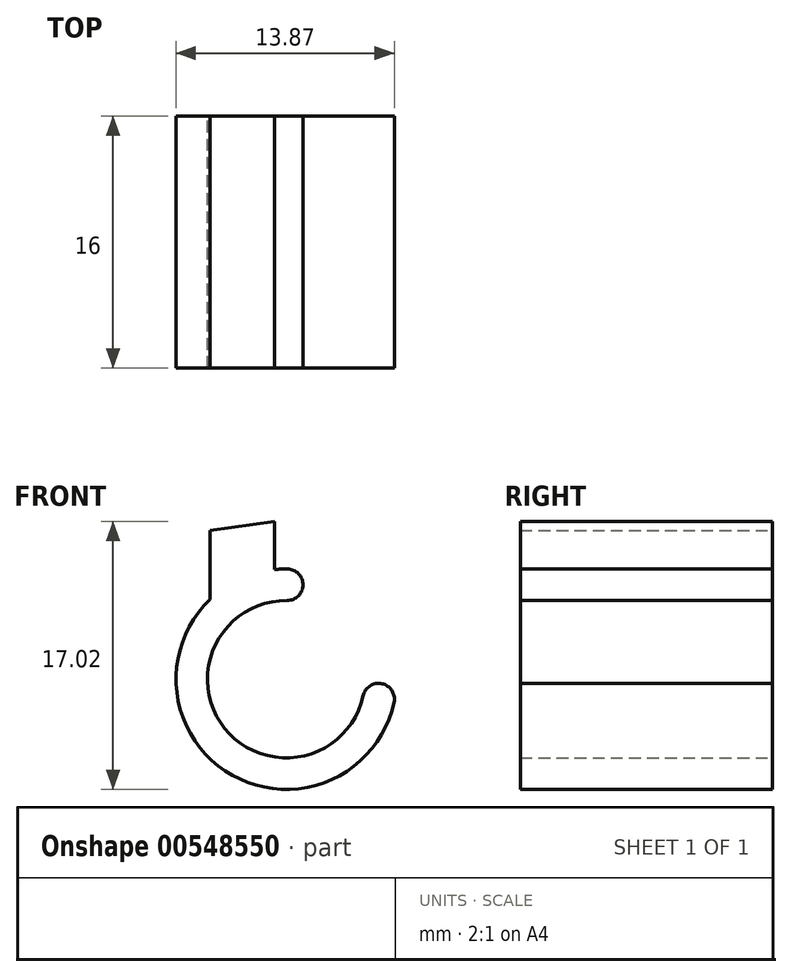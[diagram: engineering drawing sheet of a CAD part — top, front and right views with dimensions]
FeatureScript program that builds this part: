
annotation { "Feature Type Name" : "Feature", "Feature Type Description" : "" }
export const myFeature = defineFeature(function(context is Context, id is Id, definition is map)
    precondition{}
    {
        {
            var Q0;
            Q0=qCreatedBy(makeId("Front.planeOp"),FACE);
            var sketch = newSketch(context, id + "F0", { "sketchPlane" : qUnion([Q0])});
            skArc(sketch, "E0", {"start": v(61.08, 38.74) * mm, "mid": v(57.12, 30.62) * mm, "end": v(65.91, 32.69) * mm});
            skArc(sketch, "E1.0", {"start": v(61.1, 40.74) * mm, "mid": v(55.55, 29.37) * mm, "end": v(67.87, 32.27) * mm});
            skCircle(sketch, "E2", {"center": v(66.89, 32.48) * mm, "radius": 1 * mm});
            skCircle(sketch, "E3", {"center": v(61.1, 39.74) * mm, "radius": 1 * mm});
            skLineSegment(sketch, "E4", {"start": v(56.2, 38.81) * mm, "end": v(56.2, 43.19) * mm});
            skLineSegment(sketch, "E5", {"start": v(56.2, 43.19) * mm, "end": v(60.27, 43.76) * mm});
            skLineSegment(sketch, "E6", {"start": v(60.27, 43.76) * mm, "end": v(60.27, 40.7) * mm});
            skSolve(sketch);
        }
        {
            var Q0;
            {var subQ0=sQuery(id+"F0.wireOp",EDGE,"E4");Q0=makeQuery(id+"F0.imprint","IMPRINT",FACE,{"disambiguationData":[TD([[makeQuery(id+"F0.imprint","IMPRINT",EDGE,{"derivedFrom":subQ0}),-1.0]])]});}
            var Q1;
            {var subQ0=sQuery(id+"F0.wireOp",EDGE,"E2");var subQ1=makeQuery(id+"F0.imprint","INTERSECT",VERTEX,{"derivedFrom":[sQuery(id+"F0.wireOp",EDGE,"E0"),subQ0]});Q1=makeQuery(id+"F0.imprint","IMPRINT",FACE,{"disambiguationData":[TD([[makeQuery(id+"F0.imprint","IMPRINT",EDGE,{"disambiguationData":[TD([[subQ1,-1.0]])],"derivedFrom":subQ0}),1.0]])]});}
            var Q2;
            {var subQ7=sQuery(id+"F0.wireOp",EDGE,"E0");Q2=makeQuery(id+"F0.imprint","IMPRINT",FACE,{"disambiguationData":[TD([[makeQuery(id+"F0.imprint","IMPRINT",EDGE,{"derivedFrom":subQ7}),-1.0]])]});}
            var Q3;
            {var subQ0=sQuery(id+"F0.wireOp",EDGE,"E3");var subQ1=makeQuery(id+"F0.imprint","INTERSECT",VERTEX,{"derivedFrom":[sQuery(id+"F0.wireOp",EDGE,"E0"),subQ0]});Q3=makeQuery(id+"F0.imprint","IMPRINT",FACE,{"disambiguationData":[TD([[makeQuery(id+"F0.imprint","IMPRINT",EDGE,{"disambiguationData":[TD([[subQ1,1.0]])],"derivedFrom":subQ0}),1.0]])]});}
            extrude(context, id + "F1", {"entities" : qUnion([Q0, Q1, Q2, Q3]), "depth" : 8 * mm, "offsetDistance" : 25 * mm, "hasSecondDirection" : true, "secondDirectionOppositeDirection" : true, "secondDirectionDepth" : 8 * mm});
        }
    });
